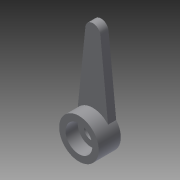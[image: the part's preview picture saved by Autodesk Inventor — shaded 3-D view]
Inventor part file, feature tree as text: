
AUTODESK INVENTOR PART (.ipt)
format: ipt  version: 2015 (Build 190159000, 159)  size: 106,496 bytes
history: native  units: mm
features: hole x3, extrude x2, sketch x2, other x1
ambient origin geometry x8: Origin, YZ Plane, XZ Plane, XY Plane, X Axis, Y Axis, Z Axis, Center Point
bodies: Body1 (feature_tree)
feature tree (8):
  other  "솔리드1"
  extrude  "돌출1"  Depth=6.8mm
  hole  "구멍1"  [1 undecoded]
  hole  "구멍2"  [1 undecoded]
  hole  "구멍3"  [1 undecoded]
  extrude  "돌출2"  Depth=19.4mm
  sketch  "스케치1"
  sketch  "스케치2"
note: 3 required parameter values undecoded (feature->parameter linkage not recoverable at this tier; creation-order binding heuristic only, values carry confidence <= 0.55)
